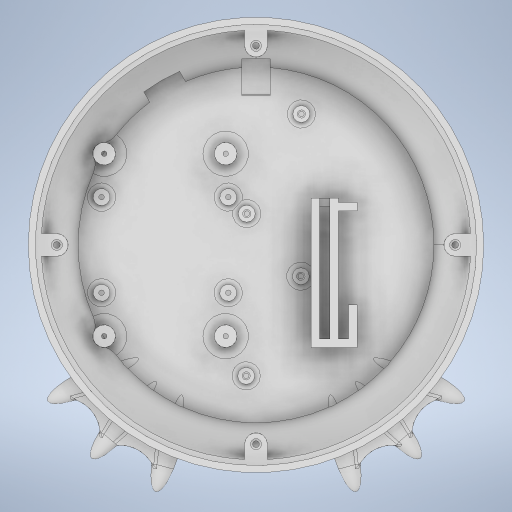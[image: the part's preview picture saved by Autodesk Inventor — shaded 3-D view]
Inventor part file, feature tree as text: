
AUTODESK INVENTOR PART (.ipt)
format: ipt  version: 2023 (Build 270158000, 158)  size: 1,302,528 bytes
history: native  units: mm
features: extrude x14, sketch x14, revolve x4, fillet x4, other x3, chamfer x3, shell x1, hole x1, pattern_circular x1, mirror x1
ambient origin geometry x8: Origin, YZ Plane, XZ Plane, XY Plane, X Axis, Y Axis, Z Axis, Center Point
bodies: Body1 (feature_tree)
feature tree (46):
  other  "솔리드1"
  revolve  "회전1"
  shell  "쉘1"  Thickness=120.0mm
  extrude  "돌출10"  Depth=140.0mm
  extrude  "돌출11"  Depth=60.0mm
  chamfer  "모따기1"  Distance=130.0mm
  hole  "구멍5"  [1 undecoded]
  pattern_circular  "원형 패턴1"  Angle=360.0deg  [1 undecoded]
  sketch  "스케치24"
  extrude  "돌출12"  Depth=4.0mm
  extrude  "돌출13"  Depth=5.0mm TaperAngle=0.0deg
  other  "작업 평면3"
  extrude  "돌출14"  Depth=155.0mm
  other  "작업 평면4"
  sketch  "스케치26"
  extrude  "돌출15"  Depth=8.0mm
  extrude  "돌출16"  Depth=70.0mm
  extrude  "돌출17"  Depth=10.0mm TaperAngle=0.0deg
  extrude  "돌출18"  Depth=8.25mm TaperAngle=45.0deg
  extrude  "돌출19"  Depth=40.0mm TaperAngle=360.0deg
  chamfer  "모따기2"  Distance=50.7mm
  fillet  "모깎기2"  Radius=38.7mm
  fillet  "모깎기3"  Radius=32.0mm
  extrude  "돌출20"  Depth=2.0mm
  chamfer  "모따기3"  Distance=33.6mm
  extrude  "돌출21"  Depth=44.5mm
  sketch  "스케치33"
  revolve  "회전3"
  revolve  "회전4"
  revolve  "회전5"
  extrude  "돌출24"  Depth=6.0mm
  extrude  "돌출25"  Depth=6.0mm
  fillet  "모깎기4"  Radius=6.0mm
  fillet  "모깎기5"  Radius=6.0mm
  mirror  "미러1"
  sketch  "스케치1"
  sketch  "스케치21"
  sketch  "스케치22"
  sketch  "스케치23"
  sketch  "스케치25"
  sketch  "스케치27"
  sketch  "스케치28"
  sketch  "스케치30"
  sketch  "스케치31"
  sketch  "스케치32"
  sketch  "스케치34"
note: 2 required parameter values undecoded (feature->parameter linkage not recoverable at this tier; creation-order binding heuristic only, values carry confidence <= 0.55)
